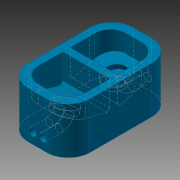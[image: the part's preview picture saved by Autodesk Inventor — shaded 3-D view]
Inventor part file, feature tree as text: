
AUTODESK INVENTOR PART (.ipt)
format: ipt  version: 2015 (Build 190159000, 159)  size: 221,696 bytes
history: native  units: in
note: dims shown in document units (in); Inventor stores cm internally (conversion verified against a paired STEP export)
features: mirror x5, extrude x4, sketch x4, plane x2, fillet x2, revolve x1
ambient origin geometry x8: Origin, YZ Plane, XZ Plane, XY Plane, X Axis, Y Axis, Z Axis, Center Point
bodies: Solid1 (feature_tree)
feature tree (18):
  extrude  "Extrusion1"  TaperAngle=105.0deg  [1 undecoded]
  extrude  "Extrusion2"  Depth=0.38in TaperAngle=0.0deg
  plane  "Work Plane1"
  mirror  "Mirror1"
  plane  "Work Plane2"
  extrude  "Extrusion3"  Depth=0.06in
  mirror  "Mirror2"
  revolve  "Revolution1"  [1 undecoded]
  mirror  "Mirror3"
  extrude  "Extrusion5"  Depth=0.04in
  mirror  "Mirror8"
  mirror  "Mirror9"
  fillet  "Fillet4"  Radius=0.06in
  fillet  "Fillet5"  [1 undecoded]
  sketch  "Sketch2"  dims[d0=0.425in d1=105.0deg]
  sketch  "Sketch3"  dims[d8=0.03in d10=0.38in d11=0.0in]
  sketch  "Sketch4"  dims[d12=0.06in d13=0.0in d14=0.18in]
  sketch  "Sketch6"  dims[d15=0.24in d16=0.04in d17=0.0in d18=0.04in d19=0.06in d20=75.0deg d33=0.15in d34=0.375in d35=0.03in d36=0.07in d37=0.06in d38=1.0in d39=0.0in d41=0.125in d42=0.175in]
note: 3 required parameter values undecoded (feature->parameter linkage not recoverable at this tier; creation-order binding heuristic only, values carry confidence <= 0.55)